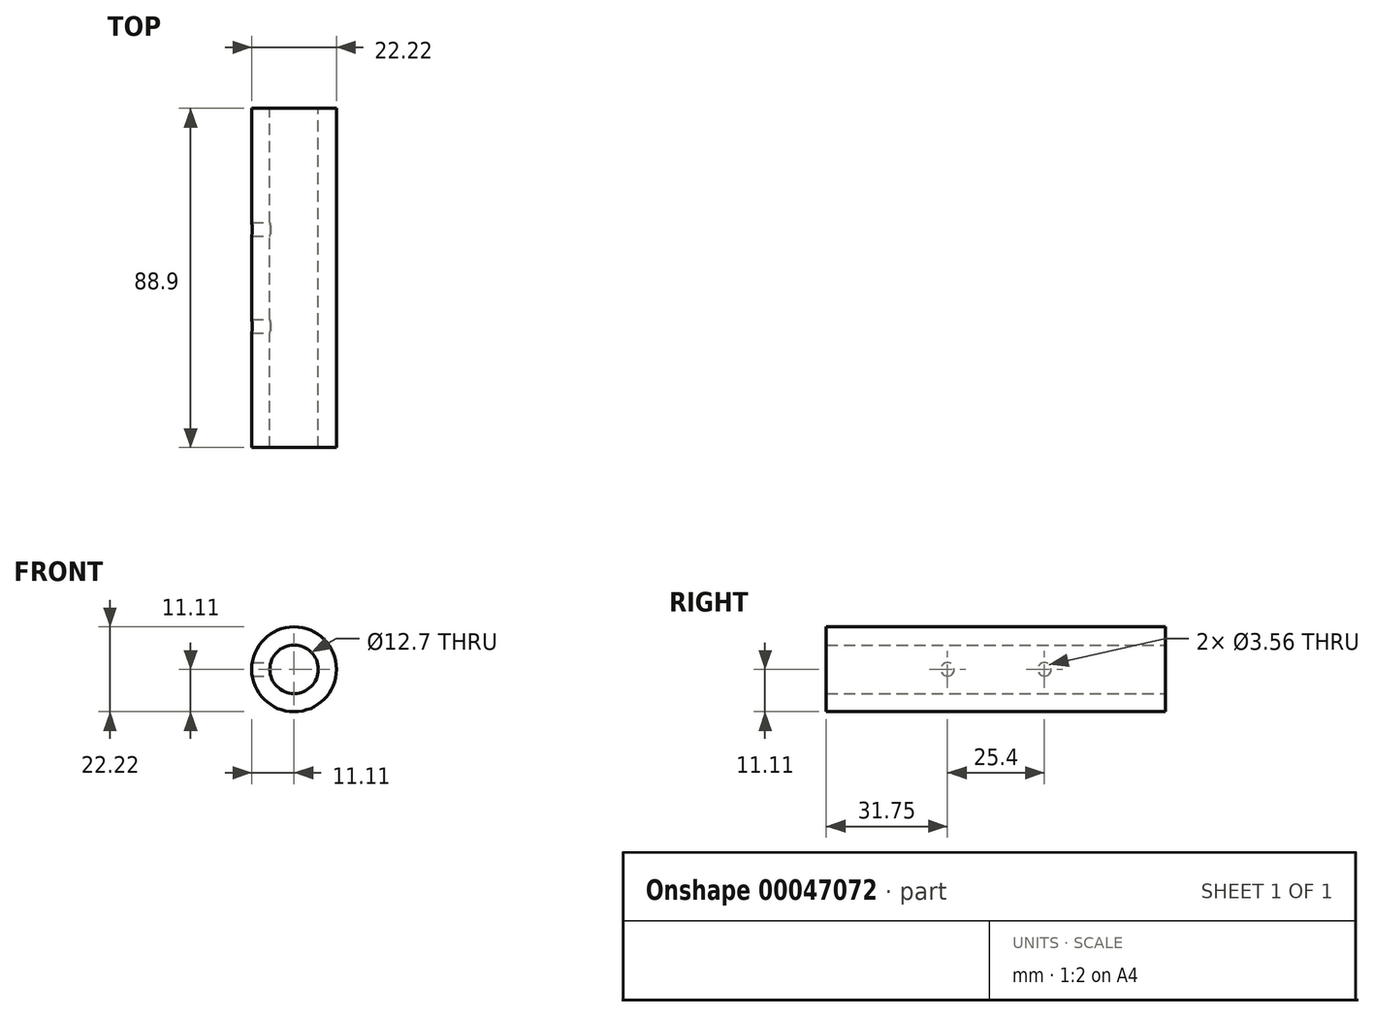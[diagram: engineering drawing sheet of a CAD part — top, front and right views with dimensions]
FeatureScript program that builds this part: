
annotation { "Feature Type Name" : "Feature", "Feature Type Description" : "" }
export const myFeature = defineFeature(function(context is Context, id is Id, definition is map)
    precondition{}
    {
        {
            var Q0;
            Q0=qCreatedBy(makeId("Front.planeOp"),FACE);
            var sketch = newSketch(context, id + "F0", { "sketchPlane" : qUnion([Q0])});
            skCircle(sketch, "E0", {"center": v(0, 0) * mm, "radius": 11.11 * mm});
            skCircle(sketch, "E1", {"center": v(0, 0) * mm, "radius": 6.35 * mm});
            skSolve(sketch);
        }
        {
            var Q0;
            Q0=makeQuery(id+"F0.imprint","IMPRINT",FACE,{"disambiguationData":[TD([[makeQuery(id+"F0.imprint","IMPRINT",EDGE,{"derivedFrom":sQuery(id+"F0.wireOp",EDGE,"E0")}),1.0]])]});
            extrude(context, id + "F1", {"entities" : qUnion([Q0]), "endBound" : BoundingType.SYMMETRIC, "depth" : 88.9 * mm});
        }
        {
            var Q0;
            Q0=qCreatedBy(makeId("Right.planeOp"),FACE);
            cPlane(context, id + "F2", {"entities" : qUnion([Q0]), "cplaneType" : CPlaneType.OFFSET, "offset" : .875 / 50.8 * mm, "width" : 152.4 * mm, "height" : 152.4 * mm});
        }
        {
            var Q0;
            Q0=qCreatedBy(id+"F2.planeOp",FACE);
            var sketch = newSketch(context, id + "F3", { "sketchPlane" : qUnion([Q0])});
            skCircle(sketch, "E2", {"center": v(-12.7, 0) * mm, "radius": 1.78 * mm});
            skLineSegment(sketch, "E3", {"start": v(0, 40.94) * mm, "end": v(0, -35.48) * mm, "construction": true});
            skCircle(sketch, "E4.MirrorC", {"center": v(12.7, 0) * mm, "radius": 1.78 * mm});
            skSolve(sketch);
        }
        {
            var Q0;
            Q0 = qSketchRegion(id + "F3", true);
            extrude(context, id + "F4", {"entities" : qUnion([Q0]), "operationType" : NewBodyOperationType.REMOVE, "endBound" : BoundingType.THROUGH_ALL, "oppositeDirection" : true, "depth" : 25.4 * mm});
        }
    });
